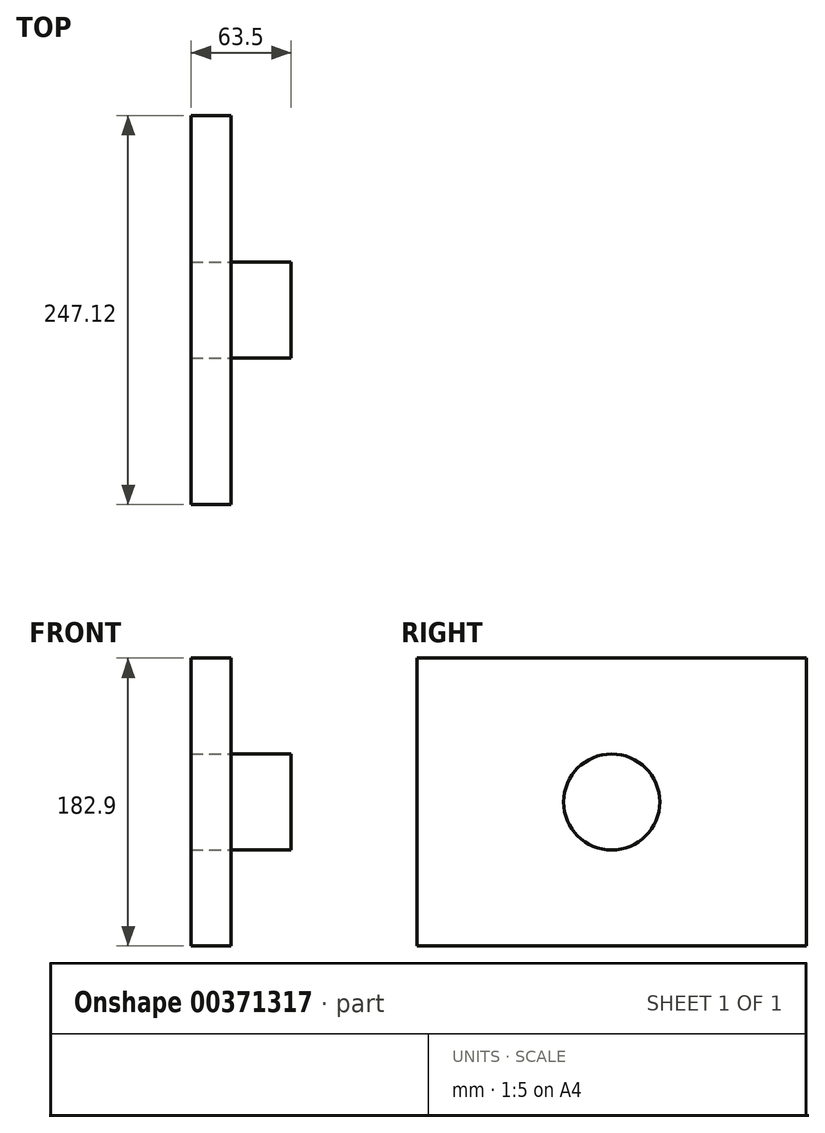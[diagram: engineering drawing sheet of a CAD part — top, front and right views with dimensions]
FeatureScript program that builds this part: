
annotation { "Feature Type Name" : "Feature", "Feature Type Description" : "" }
export const myFeature = defineFeature(function(context is Context, id is Id, definition is map)
    precondition{}
    {
        {
            var Q0;
            Q0=qCreatedBy(makeId("Right.planeOp"),FACE);
            var sketch = newSketch(context, id + "F0", { "sketchPlane" : qUnion([Q0])});
            skCircle(sketch, "E0", {"center": v(0, 0) * mm, "radius": 30.51 * mm});
            skSolve(sketch);
        }
        {
            var Q0;
            Q0=sQuery(id+"F0.wireOp",EDGE,"E0");
            extrude(context, id + "F1", {"bodyType" : ToolBodyType.SURFACE, "surfaceEntities" : qUnion([Q0]), "depth" : 63.5 * mm, "offsetDistance" : 25.4 * mm});
        }
        {
            var Q0;
            Q0=qCreatedBy(makeId("Right.planeOp"),FACE);
            var sketch = newSketch(context, id + "F2", { "sketchPlane" : qUnion([Q0])});
            skLineSegment(sketch, "E1.bottom", {"start": v(123.56, 91.45) * mm, "end": v(-123.56, 91.45) * mm});
            skLineSegment(sketch, "E1.top", {"start": v(123.56, -91.45) * mm, "end": v(-123.56, -91.45) * mm});
            skLineSegment(sketch, "E1.left", {"start": v(123.56, 91.45) * mm, "end": v(123.56, -91.45) * mm});
            skLineSegment(sketch, "E1.right", {"start": v(-123.56, 91.45) * mm, "end": v(-123.56, -91.45) * mm});
            skPoint(sketch, "E1.middle", {"position": v(0, 0) * mm});
            skSolve(sketch);
        }
        {
            var Q0;
            Q0=sQuery(id+"F2.wireOp",EDGE,"E1.bottom");
            var Q1;
            Q1=sQuery(id+"F2.wireOp",EDGE,"E1.right");
            var Q2;
            Q2=sQuery(id+"F2.wireOp",EDGE,"E1.top");
            var Q3;
            Q3=sQuery(id+"F2.wireOp",EDGE,"E1.left");
            extrude(context, id + "F3", {"bodyType" : ToolBodyType.SURFACE, "surfaceEntities" : qUnion([Q0, Q1, Q2, Q3]), "depth" : 25.4 * mm, "offsetDistance" : 25.4 * mm});
        }
    });
